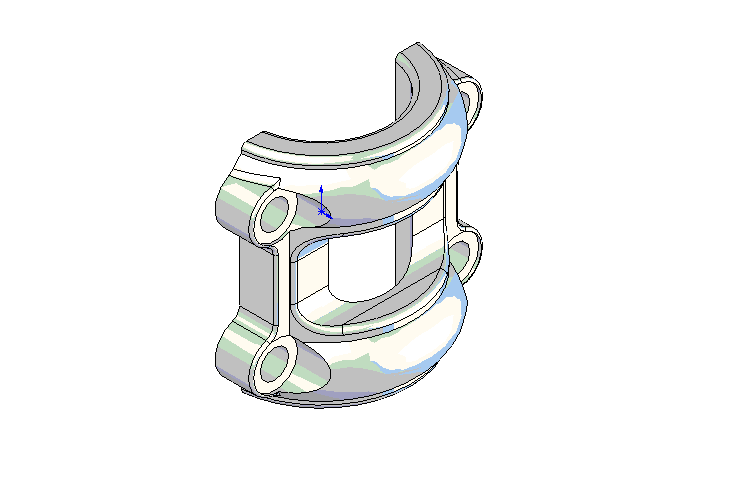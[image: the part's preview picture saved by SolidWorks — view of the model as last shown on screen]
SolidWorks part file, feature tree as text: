
SOLIDWORKS PART (.sldprt)
format: sldprt  version: not decoded by parser v0  size: 742,912 bytes
history: native  units: mm
features: sketch x7, cut_extrude x5, plane x3, fillet x3, material x1, revolve x1, extrude x1 (+10 scaffold rows collapsed)
feature tree (31):
  scaffold x10  (default folders/planes/origin — collapsed)
  material  "Matériau <non spécifié>"
  plane  "Plan de face"
  plane  "Plan de dessus"
  plane  "Plan de droite"
  sketch  "Esquisse1"  dims[D3=12.0mm D1=35.0mm D2=42.0mm D4=29.0mm D5=28.0mm]
  revolve  "Révolution1"  Angle=90deg
  sketch  "Esquisse3"  dims[D1=15.5mm]
  cut_extrude  "Enlèv. mat.-Extru.2"  [1 undecoded]
  sketch  "Esquisse2"  dims[D1=25.0mm]
  cut_extrude  "Enlèv. mat.-Extru.1"  [1 undecoded]
  sketch  "Esquisse4"  dims[c1.D2=~6.850585mm c1.D3=10.0mm c1.D1=25.0mm c2.D2=35.0mm c2.D4=35.5mm]
  extrude  "Extrusion1"  Depth=7mm
  sketch  "Esquisse5"  dims[D1=5.5mm]
  cut_extrude  "Enlèv. mat.-Extru.3"  [1 undecoded]
  sketch  "Esquisse6"  dims[D1=9.0mm]
  cut_extrude  "Enlèv. mat.-Extru.4"  [1 undecoded]
  sketch  "Esquisse7"  dims[D2=4.0mm D1=7.5mm D3=15.0mm]
  cut_extrude  "Enlèv. mat.-Extru.5"  [1 undecoded]
  fillet  "Congé1"  Radius=1mm
  fillet  "Congé2"  Radius=2mm
  fillet  "Congé3"  Radius=0.5mm
decode coverage: 12 of 17 modeling features carry decoded parameters
note: ~ marks probable driven/reference dimensions
note: 5 parameter values undecoded
summary: no parameter record found for 5 features
note: suppression state not decoded; provenance and decode notes live in map.json
